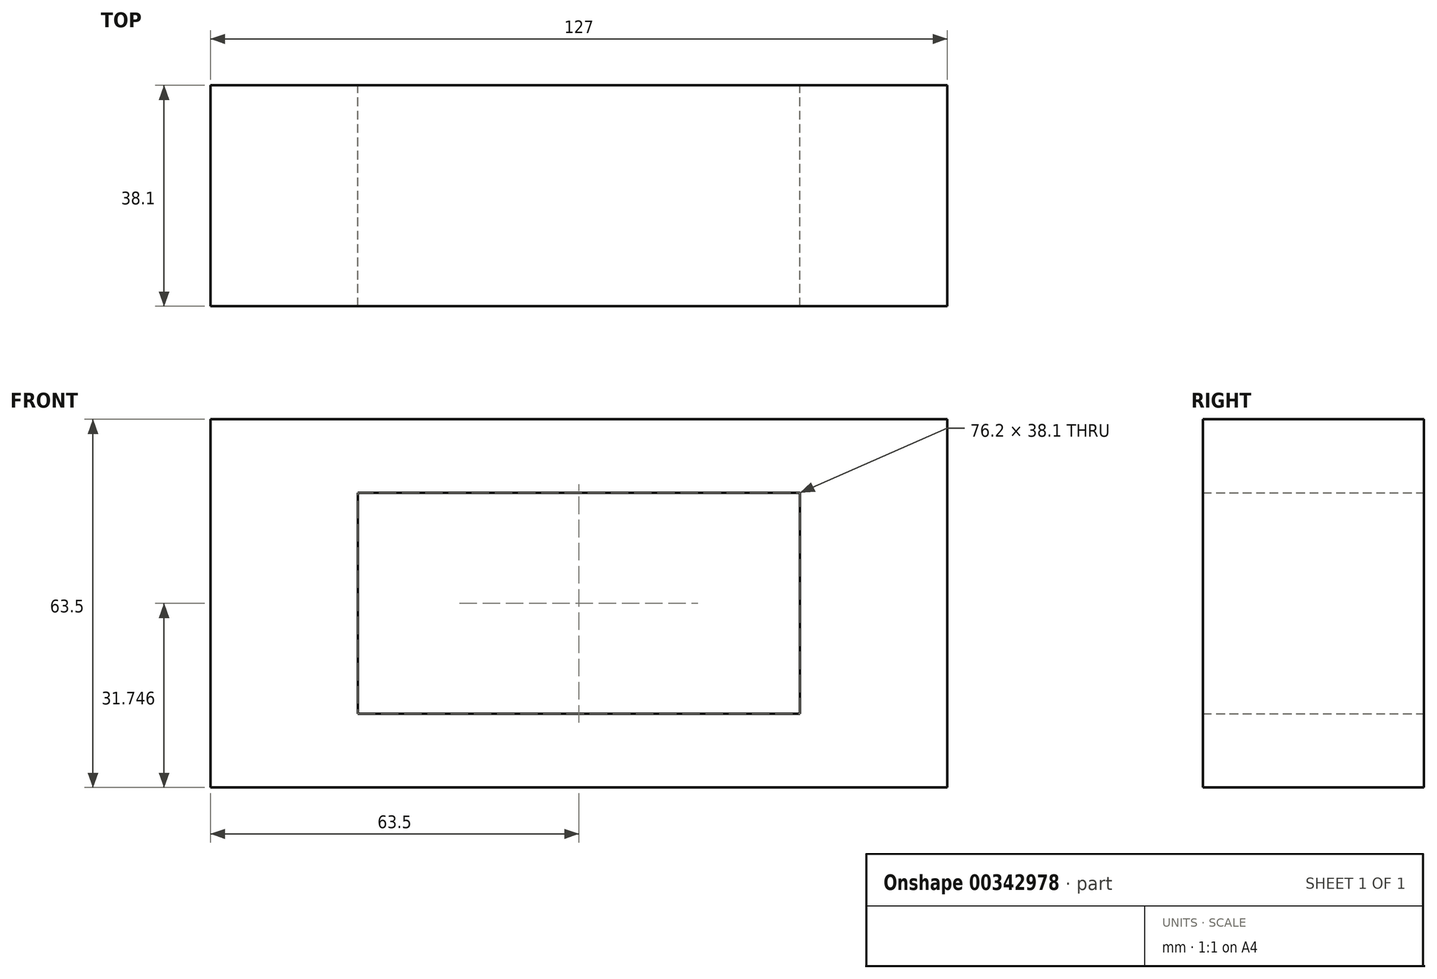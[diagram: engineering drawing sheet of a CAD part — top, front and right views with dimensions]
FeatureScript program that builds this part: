
annotation { "Feature Type Name" : "Feature", "Feature Type Description" : "" }
export const myFeature = defineFeature(function(context is Context, id is Id, definition is map)
    precondition{}
    {
        {
            var Q0;
            Q0=qCreatedBy(makeId("Front.planeOp"),FACE);
            var sketch = newSketch(context, id + "F0", { "sketchPlane" : qUnion([Q0])});
            skLineSegment(sketch, "E0", {"start": v(-63.5, -31.33) * mm, "end": v(63.5, -31.33) * mm});
            skLineSegment(sketch, "E1", {"start": v(63.5, -31.33) * mm, "end": v(63.5, 32.17) * mm});
            skLineSegment(sketch, "E2", {"start": v(-63.5, -31.33) * mm, "end": v(-63.5, 32.17) * mm});
            skLineSegment(sketch, "E3", {"start": v(-63.5, 32.17) * mm, "end": v(63.5, 32.17) * mm});
            skLineSegment(sketch, "E4", {"start": v(-38.1, 19.47) * mm, "end": v(-38.1, -18.63) * mm});
            skLineSegment(sketch, "E5", {"start": v(-38.1, -18.63) * mm, "end": v(38.1, -18.63) * mm});
            skLineSegment(sketch, "E6", {"start": v(38.1, -18.63) * mm, "end": v(38.1, 19.47) * mm});
            skLineSegment(sketch, "E7", {"start": v(38.1, 19.47) * mm, "end": v(-38.1, 19.47) * mm});
            skSolve(sketch);
        }
        {
            var Q0;
            Q0 = qSketchRegion(id + "F0", true);
            extrude(context, id + "F1", {"entities" : qUnion([Q0]), "depth" : 38.1 * mm});
        }
    });
